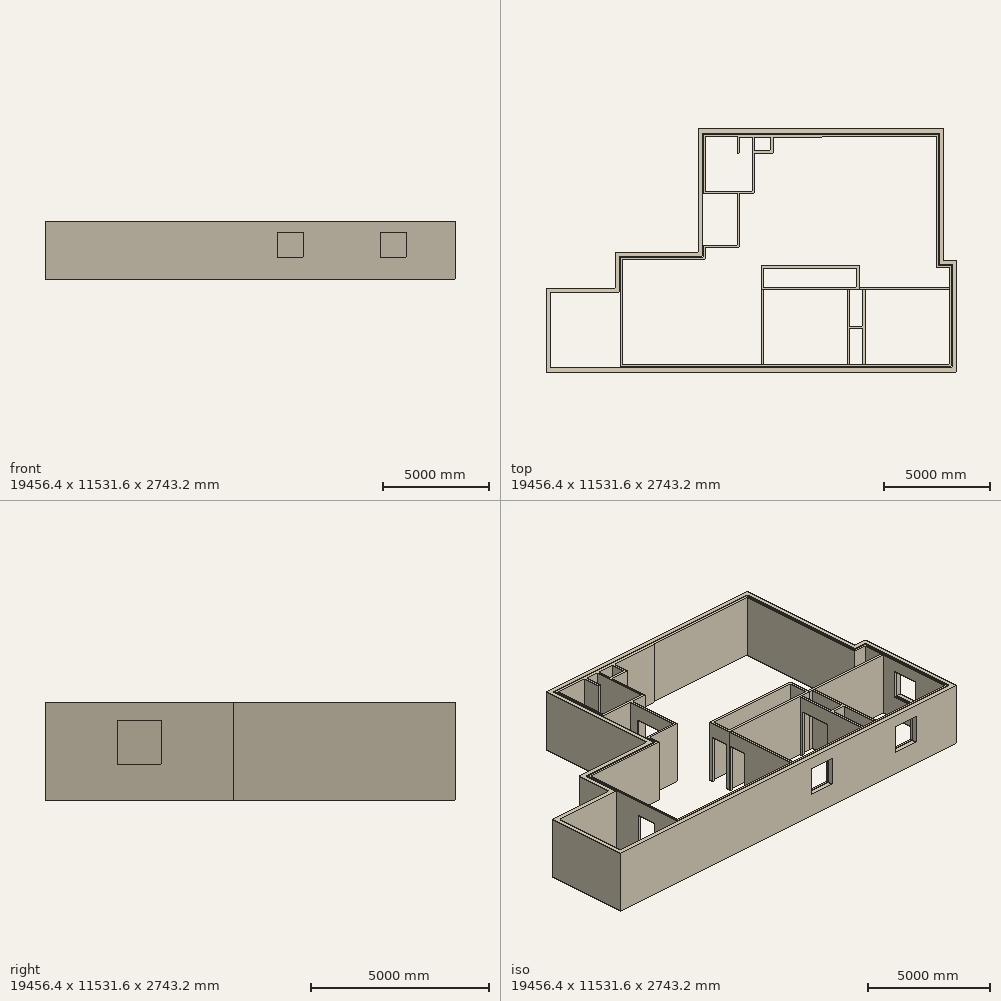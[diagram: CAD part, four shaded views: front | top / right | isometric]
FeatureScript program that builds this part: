
annotation { "Feature Type Name" : "Feature", "Feature Type Description" : "" }
export const myFeature = defineFeature(function(context is Context, id is Id, definition is map)
    precondition{}
    {
        {
            var Q0;
            Q0=qCreatedBy(makeId("Top.planeOp"),FACE);
            var sketch = newSketch(context, id + "F0", { "sketchPlane" : qUnion([Q0])});
            skLineSegment(sketch, "E0.bottom", {"start": v(0, 0) * mm, "end": v(19050, 0) * mm});
            skLineSegment(sketch, "E0.top", {"start": v(7213.6, 11125.2) * mm, "end": v(18440.4, 11125.2) * mm});
            skLineSegment(sketch, "E0.left", {"start": v(0, 0) * mm, "end": v(0, 3556) * mm});
            skLineSegment(sketch, "E0.right", {"start": v(19050, 0) * mm, "end": v(19050, 4876.8) * mm});
            skLineSegment(sketch, "E1", {"start": v(18440.4, 11125.2) * mm, "end": v(18440.4, 4876.8) * mm});
            skLineSegment(sketch, "E2", {"start": v(18440.4, 4876.8) * mm, "end": v(19050, 4876.8) * mm});
            skLineSegment(sketch, "E3", {"start": v(7213.6, 11125.2) * mm, "end": v(7213.6, 5283.2) * mm});
            skLineSegment(sketch, "E4", {"start": v(7213.6, 5283.2) * mm, "end": v(3276.6, 5283.2) * mm});
            skLineSegment(sketch, "E5", {"start": v(3276.6, 5283.2) * mm, "end": v(3276.6, 3556) * mm});
            skLineSegment(sketch, "E6", {"start": v(3276.6, 3556) * mm, "end": v(0, 3556) * mm});
            skLineSegment(sketch, "E7.bottom", {"start": v(9994.9, 4826) * mm, "end": v(14630.4, 4826) * mm, "construction": true});
            skLineSegment(sketch, "E7.top", {"start": v(9994.9, 3708.4) * mm, "end": v(14630.4, 3708.4) * mm, "construction": true});
            skLineSegment(sketch, "E7.left", {"start": v(9994.9, 4826) * mm, "end": v(9994.9, 3708.4) * mm, "construction": true});
            skLineSegment(sketch, "E7.right", {"start": v(14630.4, 4826) * mm, "end": v(14630.4, 3708.4) * mm, "construction": true});
            skPoint(sketch, "E8", {"position": v(16916.4, 0) * mm});
            skPoint(sketch, "E9", {"position": v(15697.2, 0) * mm});
            skPoint(sketch, "E10", {"position": v(12039.6, 0) * mm});
            skPoint(sketch, "E11", {"position": v(10820.4, 0) * mm});
            skPoint(sketch, "E12", {"position": v(12039.6, 11125.2) * mm});
            skPoint(sketch, "E13", {"position": v(10820.4, 11125.2) * mm});
            skPoint(sketch, "E14", {"position": v(19050, 1828.8) * mm});
            skPoint(sketch, "E15", {"position": v(19050, 3048) * mm});
            skLineSegment(sketch, "E16.0", {"start": v(7010.4, 11328.4) * mm, "end": v(18643.6, 11328.4) * mm});
            skLineSegment(sketch, "E17.0", {"start": v(18643.6, 11328.4) * mm, "end": v(18643.6, 5080) * mm});
            skLineSegment(sketch, "E18.0", {"start": v(18643.6, 5080) * mm, "end": v(19253.2, 5080) * mm});
            skLineSegment(sketch, "E19.0", {"start": v(19253.2, -203.2) * mm, "end": v(19253.2, 5080) * mm});
            skLineSegment(sketch, "E20.0", {"start": v(-203.2, -203.2) * mm, "end": v(19253.2, -203.2) * mm});
            skLineSegment(sketch, "E21.0", {"start": v(-203.2, -203.2) * mm, "end": v(-203.2, 3759.2) * mm});
            skLineSegment(sketch, "E22.0", {"start": v(3073.4, 3759.2) * mm, "end": v(-203.2, 3759.2) * mm});
            skLineSegment(sketch, "E23.0", {"start": v(3073.4, 5486.4) * mm, "end": v(3073.4, 3759.2) * mm});
            skLineSegment(sketch, "E24.0", {"start": v(7010.4, 5486.4) * mm, "end": v(3073.4, 5486.4) * mm});
            skLineSegment(sketch, "E25.0", {"start": v(7010.4, 11328.4) * mm, "end": v(7010.4, 5486.4) * mm});
            skPoint(sketch, "E26", {"position": v(8585.2, 11010.9) * mm});
            skPoint(sketch, "E27", {"position": v(9309.1, 10909.3) * mm});
            skPoint(sketch, "E28", {"position": v(8534.4, 10604.5) * mm});
            skSolve(sketch);
        }
        {
            var Q0;
            Q0=qCreatedBy(makeId("Top.planeOp"),FACE);
            var sketch = newSketch(context, id + "F1", { "sketchPlane" : qUnion([Q0])});
            skLineSegment(sketch, "E29", {"start": v(10972.8, 12242.8) * mm, "end": v(10795, 11328.4) * mm});
            skLineSegment(sketch, "E30", {"start": v(10795, 11328.4) * mm, "end": v(12065, 11328.4) * mm});
            skLineSegment(sketch, "E31", {"start": v(12065, 11328.4) * mm, "end": v(11887.2, 12242.8) * mm});
            skLineSegment(sketch, "E32", {"start": v(11887.2, 12242.8) * mm, "end": v(10972.8, 12242.8) * mm});
            skLineSegment(sketch, "E33", {"start": v(10820.4, 11125.2) * mm, "end": v(12039.6, 11125.2) * mm, "construction": true});
            skLineSegment(sketch, "E34", {"start": v(11430, 12242.8) * mm, "end": v(11430, 11125.2) * mm, "construction": true});
            skLineSegment(sketch, "E35", {"start": v(19050, 1828.8) * mm, "end": v(19050, 3048) * mm, "construction": true});
            skLineSegment(sketch, "E36", {"start": v(19253.2, 3073.4) * mm, "end": v(19253.2, 1803.4) * mm});
            skLineSegment(sketch, "E37", {"start": v(19253.2, 1803.4) * mm, "end": v(20167.6, 1981.2) * mm});
            skLineSegment(sketch, "E38", {"start": v(20167.6, 1981.2) * mm, "end": v(20167.6, 2895.6) * mm});
            skLineSegment(sketch, "E39", {"start": v(20167.6, 2895.6) * mm, "end": v(19253.2, 3073.4) * mm});
            skLineSegment(sketch, "E40", {"start": v(19050, 2438.4) * mm, "end": v(19253.2, 2438.4) * mm, "construction": true});
            skLineSegment(sketch, "E41", {"start": v(15697.2, 0) * mm, "end": v(16916.4, 0) * mm, "construction": true});
            skLineSegment(sketch, "E42", {"start": v(16306.8, 0) * mm, "end": v(16306.8, -203.2) * mm, "construction": true});
            skLineSegment(sketch, "E43", {"start": v(15671.8, -203.2) * mm, "end": v(16941.8, -203.2) * mm});
            skLineSegment(sketch, "E44", {"start": v(16941.8, -203.2) * mm, "end": v(16764, -1117.6) * mm});
            skLineSegment(sketch, "E45", {"start": v(16764, -1117.6) * mm, "end": v(15849.6, -1117.6) * mm});
            skLineSegment(sketch, "E46", {"start": v(15849.6, -1117.6) * mm, "end": v(15671.8, -203.2) * mm});
            skLineSegment(sketch, "E47", {"start": v(10820.4, 0) * mm, "end": v(12039.6, 0) * mm, "construction": true});
            skLineSegment(sketch, "E48", {"start": v(10795, -203.2) * mm, "end": v(10972.8, -1117.6) * mm});
            skLineSegment(sketch, "E49", {"start": v(10972.8, -1117.6) * mm, "end": v(11887.2, -1117.6) * mm});
            skLineSegment(sketch, "E50", {"start": v(11887.2, -1117.6) * mm, "end": v(12065, -203.2) * mm});
            skLineSegment(sketch, "E51", {"start": v(12065, -203.2) * mm, "end": v(10795, -203.2) * mm});
            skLineSegment(sketch, "E52", {"start": v(11430, 0) * mm, "end": v(11430, -203.2) * mm, "construction": true});
            skSolve(sketch);
        }
        {
            var Q0;
            Q0=makeQuery(id+"F0.imprint","IMPRINT",FACE,{"disambiguationData":[TD([[makeQuery(id+"F0.imprint","IMPRINT",EDGE,{"derivedFrom":sQuery(id+"F0.wireOp",EDGE,"E0.bottom")}),-1.0]])]});
            extrude(context, id + "F2", {"entities" : qUnion([Q0]), "depth" : 2743.2 * mm});
        }
        {
            var Q0;
            Q0=qCreatedBy(makeId("Top.planeOp"),FACE);
            var sketch = newSketch(context, id + "F3", { "sketchPlane" : qUnion([Q0])});
            skLineSegment(sketch, "E53.bottom", {"start": v(10096.5, 4724.4) * mm, "end": v(14528.8, 4724.4) * mm});
            skLineSegment(sketch, "E53.top", {"start": v(10096.5, 3810) * mm, "end": v(14528.8, 3810) * mm});
            skLineSegment(sketch, "E53.left", {"start": v(10096.5, 4724.4) * mm, "end": v(10096.5, 3810) * mm});
            skLineSegment(sketch, "E53.right", {"start": v(14528.8, 4724.4) * mm, "end": v(14528.8, 3810) * mm});
            skLineSegment(sketch, "E54.bottom", {"start": v(9982.2, 4838.7) * mm, "end": v(14643.1, 4838.7) * mm});
            skLineSegment(sketch, "E54.top", {"start": v(9982.2, 3695.7) * mm, "end": v(14643.1, 3695.7) * mm});
            skLineSegment(sketch, "E54.left", {"start": v(9982.2, 4838.7) * mm, "end": v(9982.2, 3695.7) * mm});
            skLineSegment(sketch, "E54.right", {"start": v(14643.1, 4838.7) * mm, "end": v(14643.1, 3695.7) * mm});
            skSolve(sketch);
        }
        {
            var Q0;
            Q0=qSketchRegion(id+"F3",true);
            extrude(context, id + "F4", {"entities" : qUnion([Q0]), "depth" : 2743.2 * mm});
        }
        {
            var Q0;
            Q0=qCreatedBy(makeId("Top.planeOp"),FACE);
            var sketch = newSketch(context, id + "F5", { "sketchPlane" : qUnion([Q0])});
            skLineSegment(sketch, "E55", {"start": v(3314.7, 5245.1) * mm, "end": v(3314.7, 38.1) * mm});
            skLineSegment(sketch, "E56", {"start": v(3314.7, 38.1) * mm, "end": v(19011.9, 38.1) * mm});
            skLineSegment(sketch, "E57", {"start": v(19011.9, 38.1) * mm, "end": v(19011.9, 4838.7) * mm});
            skLineSegment(sketch, "E58", {"start": v(19011.9, 4838.7) * mm, "end": v(18402.3, 4838.7) * mm});
            skLineSegment(sketch, "E59", {"start": v(18402.3, 4838.7) * mm, "end": v(18402.3, 11087.1) * mm});
            skLineSegment(sketch, "E60", {"start": v(18402.3, 11087.1) * mm, "end": v(7251.7, 11087.1) * mm});
            skLineSegment(sketch, "E61", {"start": v(7251.7, 11087.1) * mm, "end": v(7251.7, 8280.4) * mm});
            skLineSegment(sketch, "E62", {"start": v(7251.7, 8280.4) * mm, "end": v(8839.2, 8280.4) * mm});
            skLineSegment(sketch, "E63", {"start": v(8839.2, 8280.4) * mm, "end": v(8839.2, 5791.2) * mm});
            skLineSegment(sketch, "E64", {"start": v(8839.2, 5791.2) * mm, "end": v(7251.7, 5791.2) * mm});
            skLineSegment(sketch, "E65", {"start": v(7251.7, 5791.2) * mm, "end": v(7251.7, 5245.1) * mm});
            skLineSegment(sketch, "E66", {"start": v(7251.7, 5245.1) * mm, "end": v(3314.7, 5245.1) * mm});
            skLineSegment(sketch, "E67.0", {"start": v(18300.7, 10985.5) * mm, "end": v(7353.3, 10985.5) * mm});
            skLineSegment(sketch, "E67.1", {"start": v(7353.3, 5689.6) * mm, "end": v(7353.3, 5143.5) * mm});
            skLineSegment(sketch, "E67.2", {"start": v(8940.8, 5689.6) * mm, "end": v(7353.3, 5689.6) * mm});
            skLineSegment(sketch, "E67.3", {"start": v(8940.8, 8382) * mm, "end": v(8940.8, 5689.6) * mm});
            skLineSegment(sketch, "E67.4", {"start": v(7353.3, 8382) * mm, "end": v(8940.8, 8382) * mm});
            skLineSegment(sketch, "E67.5", {"start": v(7353.3, 5143.5) * mm, "end": v(3416.3, 5143.5) * mm});
            skLineSegment(sketch, "E67.6", {"start": v(7353.3, 10985.5) * mm, "end": v(7353.3, 8382) * mm});
            skLineSegment(sketch, "E67.7", {"start": v(3416.3, 5143.5) * mm, "end": v(3416.3, 139.7) * mm});
            skLineSegment(sketch, "E67.8", {"start": v(3416.3, 139.7) * mm, "end": v(18910.3, 139.7) * mm});
            skLineSegment(sketch, "E67.9", {"start": v(18910.3, 139.7) * mm, "end": v(18910.3, 4737.1) * mm});
            skLineSegment(sketch, "E67.10", {"start": v(18910.3, 4737.1) * mm, "end": v(18300.7, 4737.1) * mm});
            skLineSegment(sketch, "E67.11", {"start": v(18300.7, 4737.1) * mm, "end": v(18300.7, 10985.5) * mm});
            skSolve(sketch);
        }
        {
            var Q0;
            Q0=qSketchRegion(id+"F5",true);
            extrude(context, id + "F6", {"entities" : qUnion([Q0]), "depth" : 2743.2 * mm});
        }
        {
            var Q0;
            Q0=qCreatedBy(makeId("Top.planeOp"),FACE);
            var sketch = newSketch(context, id + "F7", { "sketchPlane" : qUnion([Q0])});
            skLineSegment(sketch, "E68", {"start": v(8940.8, 8382) * mm, "end": v(9569.45, 8382) * mm});
            skLineSegment(sketch, "E69", {"start": v(9569.45, 8382) * mm, "end": v(9569.45, 10934.7) * mm});
            skLineSegment(sketch, "E70", {"start": v(9683.75, 10934.7) * mm, "end": v(9683.75, 10299.7) * mm});
            skLineSegment(sketch, "E71", {"start": v(9683.75, 8280.4) * mm, "end": v(8940.8, 8280.4) * mm});
            skLineSegment(sketch, "E72", {"start": v(8940.8, 8280.4) * mm, "end": v(8940.8, 8382) * mm});
            skLineSegment(sketch, "E73.bottom", {"start": v(8845.55, 10934.7) * mm, "end": v(8959.85, 10934.7) * mm});
            skLineSegment(sketch, "E73.top", {"start": v(8845.55, 10172.7) * mm, "end": v(8959.85, 10172.7) * mm});
            skLineSegment(sketch, "E73.left", {"start": v(8845.55, 10934.7) * mm, "end": v(8845.55, 10172.7) * mm});
            skLineSegment(sketch, "E73.right", {"start": v(8959.85, 10934.7) * mm, "end": v(8959.85, 10172.7) * mm});
            skLineSegment(sketch, "E74", {"start": v(10560.05, 10934.7) * mm, "end": v(10560.05, 10185.4) * mm});
            skLineSegment(sketch, "E75", {"start": v(10560.05, 10185.4) * mm, "end": v(9683.75, 10185.4) * mm});
            skLineSegment(sketch, "E76", {"start": v(9683.75, 10299.7) * mm, "end": v(10445.75, 10299.7) * mm});
            skLineSegment(sketch, "E77", {"start": v(10445.75, 10299.7) * mm, "end": v(10445.75, 10934.7) * mm});
            skLineSegment(sketch, "E78.bottom", {"start": v(8845.55, 10985.5) * mm, "end": v(12903.2, 10985.5) * mm});
            skLineSegment(sketch, "E78.top", {"start": v(8845.55, 10934.7) * mm, "end": v(9569.45, 10934.7) * mm});
            skLineSegment(sketch, "E78.left", {"start": v(8845.55, 10985.5) * mm, "end": v(8845.55, 10934.7) * mm});
            skLineSegment(sketch, "E78.right", {"start": v(12903.2, 10985.5) * mm, "end": v(12903.2, 10934.7) * mm});
            skLineSegment(sketch, "E79.trimOffspring", {"start": v(9683.75, 10185.4) * mm, "end": v(9683.75, 8280.4) * mm});
            skLineSegment(sketch, "E80.trimOffspring", {"start": v(10560.05, 10934.7) * mm, "end": v(12903.2, 10934.7) * mm});
            skLineSegment(sketch, "E81.trimOffspring", {"start": v(9683.75, 10934.7) * mm, "end": v(10445.75, 10934.7) * mm});
            skPoint(sketch, "E82", {"position": v(10972.8, 10934.7) * mm});
            skPoint(sketch, "E83", {"position": v(11887.2, 10934.7) * mm});
            skPoint(sketch, "E84", {"position": v(12496.8, 10934.7) * mm});
            skLineSegment(sketch, "E85.bottom", {"start": v(10560.05, 10934.7) * mm, "end": v(10972.8, 10934.7) * mm, "construction": true});
            skLineSegment(sketch, "E85.top", {"start": v(10560.05, 10325.1) * mm, "end": v(10972.8, 10325.1) * mm, "construction": true});
            skLineSegment(sketch, "E85.left", {"start": v(10560.05, 10934.7) * mm, "end": v(10560.05, 10325.1) * mm, "construction": true});
            skLineSegment(sketch, "E85.right", {"start": v(10972.8, 10934.7) * mm, "end": v(10972.8, 10325.1) * mm, "construction": true});
            skLineSegment(sketch, "E86.bottom", {"start": v(10972.8, 10934.7) * mm, "end": v(11887.2, 10934.7) * mm, "construction": true});
            skLineSegment(sketch, "E86.top", {"start": v(10972.8, 10325.1) * mm, "end": v(11887.2, 10325.1) * mm, "construction": true});
            skLineSegment(sketch, "E86.right", {"start": v(11887.2, 10934.7) * mm, "end": v(11887.2, 10325.1) * mm, "construction": true});
            skLineSegment(sketch, "E87.bottom", {"start": v(11887.2, 10934.7) * mm, "end": v(12496.8, 10934.7) * mm, "construction": true});
            skLineSegment(sketch, "E87.top", {"start": v(11887.2, 10325.1) * mm, "end": v(12496.8, 10325.1) * mm, "construction": true});
            skLineSegment(sketch, "E87.right", {"start": v(12496.8, 10934.7) * mm, "end": v(12496.8, 10325.1) * mm, "construction": true});
            skLineSegment(sketch, "E88.bottom", {"start": v(12496.8, 10934.7) * mm, "end": v(12903.2, 10934.7) * mm, "construction": true});
            skLineSegment(sketch, "E88.top", {"start": v(12496.8, 10325.1) * mm, "end": v(12903.2, 10325.1) * mm, "construction": true});
            skLineSegment(sketch, "E88.right", {"start": v(12903.2, 10934.7) * mm, "end": v(12903.2, 10325.1) * mm, "construction": true});
            skPoint(sketch, "E89", {"position": v(11430, 10325.1) * mm});
            skSolve(sketch);
        }
        {
            var Q0;
            Q0=qSketchRegion(id+"F7",true);
            var Q1;
            Q1=makeQuery(id+"F2.opExtrude","CAP_FACE",FACE,{"disambiguationData":[OSD([sQuery(id+"F0.wireOp",EDGE,"E0.bottom"),sQuery(id+"F0.wireOp",EDGE,"E0.top"),sQuery(id+"F0.wireOp",EDGE,"E0.left"),sQuery(id+"F0.wireOp",EDGE,"E0.right"),sQuery(id+"F0.wireOp",EDGE,"E1"),sQuery(id+"F0.wireOp",EDGE,"E2"),sQuery(id+"F0.wireOp",EDGE,"E3"),sQuery(id+"F0.wireOp",EDGE,"E4"),sQuery(id+"F0.wireOp",EDGE,"E5"),sQuery(id+"F0.wireOp",EDGE,"E6"),sQuery(id+"F0.wireOp",EDGE,"E16.0"),sQuery(id+"F0.wireOp",EDGE,"E17.0"),sQuery(id+"F0.wireOp",EDGE,"E18.0"),sQuery(id+"F0.wireOp",EDGE,"E19.0"),sQuery(id+"F0.wireOp",EDGE,"E20.0"),sQuery(id+"F0.wireOp",EDGE,"E21.0"),sQuery(id+"F0.wireOp",EDGE,"E22.0"),sQuery(id+"F0.wireOp",EDGE,"E23.0"),sQuery(id+"F0.wireOp",EDGE,"E24.0"),sQuery(id+"F0.wireOp",EDGE,"E25.0")])],"isStart":false});
            extrude(context, id + "F8", {"entities" : qUnion([Q0]), "operationType" : NewBodyOperationType.ADD, "endBound" : BoundingType.UP_TO_SURFACE, "endBoundEntityFace" : qUnion([Q1]), "depth" : 25.4 * mm});
        }
        {
            var Q0;
            Q0=qCreatedBy(makeId("Top.planeOp"),FACE);
            var sketch = newSketch(context, id + "F9", { "sketchPlane" : qUnion([Q0])});
            skLineSegment(sketch, "E90.bottom", {"start": v(9982.2, 3695.7) * mm, "end": v(10096.5, 3695.7) * mm});
            skLineSegment(sketch, "E90.top", {"start": v(9982.2, 139.7) * mm, "end": v(10096.5, 139.7) * mm});
            skLineSegment(sketch, "E90.left", {"start": v(9982.2, 3695.7) * mm, "end": v(9982.2, 139.7) * mm});
            skLineSegment(sketch, "E90.right", {"start": v(10096.5, 3695.7) * mm, "end": v(10096.5, 139.7) * mm});
            skLineSegment(sketch, "E91.bottom", {"start": v(14643.1, 3695.7) * mm, "end": v(18910.3, 3695.7) * mm});
            skLineSegment(sketch, "E91.top", {"start": v(14643.1, 3810) * mm, "end": v(18910.3, 3810) * mm});
            skLineSegment(sketch, "E91.left", {"start": v(14643.1, 3695.7) * mm, "end": v(14643.1, 3810) * mm});
            skLineSegment(sketch, "E91.right", {"start": v(18910.3, 3695.7) * mm, "end": v(18910.3, 3810) * mm});
            skSolve(sketch);
        }
        {
            var Q0;
            Q0=qSketchRegion(id+"F9",true);
            extrude(context, id + "F10", {"entities" : qUnion([Q0]), "depth" : 2743.2 * mm});
        }
        {
            var Q0;
            Q0=makeQuery(id+"F2.opExtrude","SWEPT_FACE",FACE,{"disambiguationData":[OSD([sQuery(id+"F0.wireOp",EDGE,"E20.0")])]});
            var sketch = newSketch(context, id + "F11", { "sketchPlane" : qUnion([Q0])});
            skLineSegment(sketch, "E92.bottom", {"start": v(10820.4, 1016) * mm, "end": v(12039.6, 1016) * mm});
            skLineSegment(sketch, "E92.top", {"start": v(10820.4, 2235.2) * mm, "end": v(12039.6, 2235.2) * mm});
            skLineSegment(sketch, "E92.left", {"start": v(10820.4, 1016) * mm, "end": v(10820.4, 2235.2) * mm});
            skLineSegment(sketch, "E92.right", {"start": v(12039.6, 1016) * mm, "end": v(12039.6, 2235.2) * mm});
            skLineSegment(sketch, "E93.bottom", {"start": v(15697.2, 1016) * mm, "end": v(16916.4, 1016) * mm});
            skLineSegment(sketch, "E93.top", {"start": v(15697.2, 2235.2) * mm, "end": v(16916.4, 2235.2) * mm});
            skLineSegment(sketch, "E93.left", {"start": v(15697.2, 1016) * mm, "end": v(15697.2, 2235.2) * mm});
            skLineSegment(sketch, "E93.right", {"start": v(16916.4, 1016) * mm, "end": v(16916.4, 2235.2) * mm});
            skSolve(sketch);
        }
        {
            var Q0;
            Q0=qSketchRegion(id+"F11",true);
            var Q1;
            Q1=makeQuery(id+"F6.opExtrude","SWEPT_FACE",FACE,{"disambiguationData":[OSD([sQuery(id+"F5.wireOp",EDGE,"E67.8")])]});
            extrude(context, id + "F12", {"entities" : qUnion([Q0]), "operationType" : NewBodyOperationType.REMOVE, "endBound" : BoundingType.UP_TO_SURFACE, "oppositeDirection" : true, "endBoundEntityFace" : qUnion([Q1]), "depth" : 25.4 * mm});
        }
        {
            var Q0;
            Q0=qCreatedBy(makeId("Top.planeOp"),FACE);
            var sketch = newSketch(context, id + "F13", { "sketchPlane" : qUnion([Q0])});
            skLineSegment(sketch, "E94", {"start": v(10096.5, 1917.7) * mm, "end": v(14503.4, 1917.7) * mm, "construction": true});
            skLineSegment(sketch, "E95", {"start": v(14503.4, 1917.7) * mm, "end": v(18910.3, 1917.7) * mm, "construction": true});
            skLineSegment(sketch, "E96", {"start": v(14503.4, 3695.7) * mm, "end": v(14503.4, 139.7) * mm, "construction": true});
            skLineSegment(sketch, "E97.bottom", {"start": v(14084.3, 3695.7) * mm, "end": v(14198.6, 3695.7) * mm});
            skLineSegment(sketch, "E97.top", {"start": v(14084.3, 139.7) * mm, "end": v(14198.6, 139.7) * mm});
            skLineSegment(sketch, "E97.left", {"start": v(14084.3, 3695.7) * mm, "end": v(14084.3, 139.7) * mm});
            skLineSegment(sketch, "E97.right", {"start": v(14198.6, 3695.7) * mm, "end": v(14198.6, 1974.85) * mm});
            skLineSegment(sketch, "E98.bottom", {"start": v(14808.2, 3695.7) * mm, "end": v(14922.5, 3695.7) * mm});
            skLineSegment(sketch, "E98.top", {"start": v(14808.2, 139.7) * mm, "end": v(14922.5, 139.7) * mm});
            skLineSegment(sketch, "E98.left", {"start": v(14808.2, 3695.7) * mm, "end": v(14808.2, 1974.85) * mm});
            skLineSegment(sketch, "E98.right", {"start": v(14922.5, 3695.7) * mm, "end": v(14922.5, 139.7) * mm});
            skLineSegment(sketch, "E99.bottom", {"start": v(14198.6, 1974.85) * mm, "end": v(14808.2, 1974.85) * mm});
            skLineSegment(sketch, "E99.top", {"start": v(14198.6, 1860.55) * mm, "end": v(14808.2, 1860.55) * mm});
            skPoint(sketch, "E100", {"position": v(14503.4, 1974.85) * mm});
            skLineSegment(sketch, "E101.trimOffspring", {"start": v(14808.2, 1860.55) * mm, "end": v(14808.2, 139.7) * mm});
            skLineSegment(sketch, "E102", {"start": v(14198.6, 1860.55) * mm, "end": v(14198.6, 139.7) * mm});
            skSolve(sketch);
        }
        {
            var Q0;
            Q0=qSketchRegion(id+"F13",true);
            var Q1;
            Q1=makeQuery(id+"F2.opExtrude","CAP_FACE",FACE,{"disambiguationData":[OSD([sQuery(id+"F0.wireOp",EDGE,"E0.bottom"),sQuery(id+"F0.wireOp",EDGE,"E0.top"),sQuery(id+"F0.wireOp",EDGE,"E0.left"),sQuery(id+"F0.wireOp",EDGE,"E0.right"),sQuery(id+"F0.wireOp",EDGE,"E1"),sQuery(id+"F0.wireOp",EDGE,"E2"),sQuery(id+"F0.wireOp",EDGE,"E3"),sQuery(id+"F0.wireOp",EDGE,"E4"),sQuery(id+"F0.wireOp",EDGE,"E5"),sQuery(id+"F0.wireOp",EDGE,"E6"),sQuery(id+"F0.wireOp",EDGE,"E16.0"),sQuery(id+"F0.wireOp",EDGE,"E17.0"),sQuery(id+"F0.wireOp",EDGE,"E18.0"),sQuery(id+"F0.wireOp",EDGE,"E19.0"),sQuery(id+"F0.wireOp",EDGE,"E20.0"),sQuery(id+"F0.wireOp",EDGE,"E21.0"),sQuery(id+"F0.wireOp",EDGE,"E22.0"),sQuery(id+"F0.wireOp",EDGE,"E23.0"),sQuery(id+"F0.wireOp",EDGE,"E24.0"),sQuery(id+"F0.wireOp",EDGE,"E25.0")])],"isStart":false});
            extrude(context, id + "F14", {"entities" : qUnion([Q0]), "endBound" : BoundingType.UP_TO_SURFACE, "endBoundEntityFace" : qUnion([Q1]), "depth" : 25.4 * mm});
        }
        {
            var Q0;
            Q0=makeQuery(id+"F14.opExtrude","SWEPT_FACE",FACE,{"disambiguationData":[OSD([sQuery(id+"F13.wireOp",EDGE,"E98.right")])]});
            var sketch = newSketch(context, id + "F15", { "sketchPlane" : qUnion([Q0])});
            skLineSegment(sketch, "E103.bottom", {"start": v(257.17, 0) * mm, "end": v(1743.07, 0) * mm});
            skLineSegment(sketch, "E103.top", {"start": v(257.17, 2082.8) * mm, "end": v(1743.07, 2082.8) * mm});
            skLineSegment(sketch, "E103.left", {"start": v(257.17, 0) * mm, "end": v(257.17, 2082.8) * mm});
            skLineSegment(sketch, "E103.right", {"start": v(1743.07, 0) * mm, "end": v(1743.07, 2082.8) * mm});
            skLineSegment(sketch, "E104", {"start": v(1743.07, 2082.8) * mm, "end": v(1860.55, 2082.8) * mm, "construction": true});
            skLineSegment(sketch, "E105", {"start": v(257.17, 2082.8) * mm, "end": v(139.7, 2082.8) * mm, "construction": true});
            skSolve(sketch);
        }
        {
            var Q0;
            Q0=qSketchRegion(id+"F15",true);
            extrude(context, id + "F16", {"entities" : qUnion([Q0]), "operationType" : NewBodyOperationType.REMOVE, "endBound" : BoundingType.UP_TO_NEXT, "oppositeDirection" : true, "depth" : 25.4 * mm});
        }
        {
            var Q0;
            Q0=makeQuery(id+"F14.opExtrude","SWEPT_FACE",FACE,{"disambiguationData":[OSD([sQuery(id+"F13.wireOp",EDGE,"E97.left")])]});
            var sketch = newSketch(context, id + "F17", { "sketchPlane" : qUnion([Q0])});
            skLineSegment(sketch, "E106.bottom", {"start": v(-3578.23, 0) * mm, "end": v(-2092.32, 0) * mm});
            skLineSegment(sketch, "E106.top", {"start": v(-3578.23, 2082.8) * mm, "end": v(-2092.32, 2082.8) * mm});
            skLineSegment(sketch, "E106.left", {"start": v(-3578.23, 0) * mm, "end": v(-3578.23, 2082.8) * mm});
            skLineSegment(sketch, "E106.right", {"start": v(-2092.32, 0) * mm, "end": v(-2092.32, 2082.8) * mm});
            skLineSegment(sketch, "E107", {"start": v(-3578.23, 2082.8) * mm, "end": v(-3695.7, 2082.8) * mm, "construction": true});
            skLineSegment(sketch, "E108", {"start": v(-2092.32, 2082.8) * mm, "end": v(-1974.85, 2082.8) * mm, "construction": true});
            skSolve(sketch);
        }
        {
            var Q0;
            Q0=qSketchRegion(id+"F17",true);
            extrude(context, id + "F18", {"entities" : qUnion([Q0]), "operationType" : NewBodyOperationType.REMOVE, "endBound" : BoundingType.UP_TO_NEXT, "oppositeDirection" : true, "depth" : 25.4 * mm});
        }
        {
            var Q0;
            Q0=qCreatedBy(makeId("Top.planeOp"),FACE);
            var sketch = newSketch(context, id + "F19", { "sketchPlane" : qUnion([Q0])});
            skArc(sketch, "E109", {"start": v(10096.5, 2844.8) * mm, "mid": v(10635.32, 3067.98) * mm, "end": v(10858.5, 3606.8) * mm, "construction": true});
            skArc(sketch, "E110", {"start": v(9982.2, 3886.2) * mm, "mid": v(9443.38, 4109.38) * mm, "end": v(9220.2, 4648.2) * mm, "construction": true});
            skLineSegment(sketch, "E111", {"start": v(10096.5, 3606.8) * mm, "end": v(10858.5, 3606.8) * mm, "construction": true});
            skLineSegment(sketch, "E112", {"start": v(10096.5, 3606.8) * mm, "end": v(10096.5, 2844.8) * mm, "construction": true});
            skLineSegment(sketch, "E113", {"start": v(9982.2, 3886.2) * mm, "end": v(9982.2, 4648.2) * mm, "construction": true});
            skLineSegment(sketch, "E114", {"start": v(9220.2, 4648.2) * mm, "end": v(9982.2, 4648.2) * mm, "construction": true});
            skLineSegment(sketch, "E115", {"start": v(9982.2, 4648.2) * mm, "end": v(9982.2, 4724.4) * mm, "construction": true});
            skLineSegment(sketch, "E116", {"start": v(9982.2, 3886.2) * mm, "end": v(9982.2, 3810) * mm, "construction": true});
            skArc(sketch, "E117", {"start": v(15836.9, 2933.7) * mm, "mid": v(16375.72, 3156.88) * mm, "end": v(16598.9, 3695.7) * mm, "construction": true});
            skArc(sketch, "E118", {"start": v(8940.8, 6985) * mm, "mid": v(9587.38, 6717.18) * mm, "end": v(9855.2, 6070.6) * mm, "construction": true});
            skArc(sketch, "E119", {"start": v(8940.8, 6985) * mm, "mid": v(9587.38, 7252.82) * mm, "end": v(9855.2, 7899.4) * mm, "construction": true});
            skLineSegment(sketch, "E120", {"start": v(8940.8, 7899.4) * mm, "end": v(9855.2, 7899.4) * mm, "construction": true});
            skLineSegment(sketch, "E121", {"start": v(8940.8, 6985) * mm, "end": v(8940.8, 7899.4) * mm, "construction": true});
            skLineSegment(sketch, "E122", {"start": v(8940.8, 6985) * mm, "end": v(8940.8, 6070.6) * mm, "construction": true});
            skLineSegment(sketch, "E123", {"start": v(8940.8, 6070.6) * mm, "end": v(9855.2, 6070.6) * mm, "construction": true});
            skLineSegment(sketch, "E124", {"start": v(15836.9, 2933.7) * mm, "end": v(15836.9, 3695.7) * mm, "construction": true});
            skLineSegment(sketch, "E125", {"start": v(15836.9, 3695.7) * mm, "end": v(16598.9, 3695.7) * mm, "construction": true});
            skArc(sketch, "E126", {"start": v(3416.3, 2273.3) * mm, "mid": v(4062.88, 2005.48) * mm, "end": v(4330.7, 1358.9) * mm, "construction": true});
            skLineSegment(sketch, "E127", {"start": v(3416.3, 2273.3) * mm, "end": v(3416.3, 1358.9) * mm, "construction": true});
            skLineSegment(sketch, "E128", {"start": v(3416.3, 1358.9) * mm, "end": v(4330.7, 1358.9) * mm, "construction": true});
            skArc(sketch, "E129", {"start": v(14643.1, 4673.6) * mm, "mid": v(15217.84, 4435.54) * mm, "end": v(15455.9, 3860.8) * mm, "construction": true});
            skLineSegment(sketch, "E130", {"start": v(15455.9, 3860.8) * mm, "end": v(14643.1, 3860.8) * mm, "construction": true});
            skLineSegment(sketch, "E131", {"start": v(14643.1, 3860.8) * mm, "end": v(14643.1, 4673.6) * mm, "construction": true});
            skLineSegment(sketch, "E132", {"start": v(14643.1, 4673.6) * mm, "end": v(14643.1, 4724.4) * mm, "construction": true});
            skLineSegment(sketch, "E133", {"start": v(14643.1, 3860.8) * mm, "end": v(14643.1, 3810) * mm, "construction": true});
            skArc(sketch, "E134", {"start": v(9569.45, 9220.2) * mm, "mid": v(9030.63, 8997.02) * mm, "end": v(8807.45, 8458.2) * mm, "construction": true});
            skLineSegment(sketch, "E135", {"start": v(8807.45, 8458.2) * mm, "end": v(9569.45, 8458.2) * mm, "construction": true});
            skLineSegment(sketch, "E136", {"start": v(9569.45, 8458.2) * mm, "end": v(9569.45, 9220.2) * mm, "construction": true});
            skArc(sketch, "E137", {"start": v(9759.95, 9575.8) * mm, "mid": v(10191, 9754.35) * mm, "end": v(10369.55, 10185.4) * mm, "construction": true});
            skLineSegment(sketch, "E138", {"start": v(9759.95, 9575.8) * mm, "end": v(9759.95, 10185.4) * mm, "construction": true});
            skLineSegment(sketch, "E139", {"start": v(9759.95, 10185.4) * mm, "end": v(10369.55, 10185.4) * mm, "construction": true});
            skSolve(sketch);
        }
        {
            var Q0;
            Q0=makeQuery(id+"F10.opExtrude","SWEPT_FACE",FACE,{"disambiguationData":[OSD([sQuery(id+"F9.wireOp",EDGE,"E90.left")])]});
            var sketch = newSketch(context, id + "F20", { "sketchPlane" : qUnion([Q0])});
            skLineSegment(sketch, "E140.bottom", {"start": v(-3606.8, 0) * mm, "end": v(-2844.8, 0) * mm});
            skLineSegment(sketch, "E140.top", {"start": v(-3606.8, 2082.8) * mm, "end": v(-2844.8, 2082.8) * mm});
            skLineSegment(sketch, "E140.left", {"start": v(-3606.8, 0) * mm, "end": v(-3606.8, 2082.8) * mm});
            skLineSegment(sketch, "E140.right", {"start": v(-2844.8, 0) * mm, "end": v(-2844.8, 2082.8) * mm});
            skSolve(sketch);
        }
        {
            var Q0;
            Q0=qSketchRegion(id+"F20",true);
            extrude(context, id + "F21", {"entities" : qUnion([Q0]), "operationType" : NewBodyOperationType.REMOVE, "endBound" : BoundingType.UP_TO_NEXT, "oppositeDirection" : true, "depth" : 25.4 * mm});
        }
        {
            var Q0;
            Q0=makeQuery(id+"F4.opExtrude","SWEPT_FACE",FACE,{"disambiguationData":[OSD([sQuery(id+"F3.wireOp",EDGE,"E54.left")])]});
            var sketch = newSketch(context, id + "F22", { "sketchPlane" : qUnion([Q0])});
            skLineSegment(sketch, "E141.bottom", {"start": v(-4648.2, 0) * mm, "end": v(-3886.2, 0) * mm});
            skLineSegment(sketch, "E141.top", {"start": v(-4648.2, 2082.8) * mm, "end": v(-3886.2, 2082.8) * mm});
            skLineSegment(sketch, "E141.left", {"start": v(-4648.2, 0) * mm, "end": v(-4648.2, 2082.8) * mm});
            skLineSegment(sketch, "E141.right", {"start": v(-3886.2, 0) * mm, "end": v(-3886.2, 2082.8) * mm});
            skSolve(sketch);
        }
        {
            var Q0;
            Q0=qSketchRegion(id+"F22",true);
            var Q1;
            Q1=makeQuery(id+"F4.opExtrude","SWEPT_FACE",FACE,{"disambiguationData":[OSD([sQuery(id+"F3.wireOp",EDGE,"E54.right")])]});
            extrude(context, id + "F23", {"entities" : qUnion([Q0]), "operationType" : NewBodyOperationType.REMOVE, "endBound" : BoundingType.UP_TO_SURFACE, "oppositeDirection" : true, "endBoundEntityFace" : qUnion([Q1]), "depth" : 25.4 * mm});
        }
        {
            var Q0;
            Q0=makeQuery(id+"F6.opExtrude","SWEPT_FACE",FACE,{"disambiguationData":[OSD([sQuery(id+"F5.wireOp",EDGE,"E67.3")])]});
            var sketch = newSketch(context, id + "F24", { "sketchPlane" : qUnion([Q0])});
            skLineSegment(sketch, "E142.bottom", {"start": v(6070.6, 0) * mm, "end": v(7899.4, 0) * mm});
            skLineSegment(sketch, "E142.top", {"start": v(6070.6, 2082.8) * mm, "end": v(7899.4, 2082.8) * mm});
            skLineSegment(sketch, "E142.left", {"start": v(6070.6, 0) * mm, "end": v(6070.6, 2082.8) * mm});
            skLineSegment(sketch, "E142.right", {"start": v(7899.4, 0) * mm, "end": v(7899.4, 2082.8) * mm});
            skSolve(sketch);
        }
        {
            var Q0;
            Q0=qSketchRegion(id+"F24",true);
            extrude(context, id + "F25", {"entities" : qUnion([Q0]), "operationType" : NewBodyOperationType.REMOVE, "endBound" : BoundingType.UP_TO_NEXT, "oppositeDirection" : true, "depth" : 25.4 * mm});
        }
        {
            var Q0;
            Q0=makeQuery(id+"F6.opExtrude","SWEPT_FACE",FACE,{"disambiguationData":[OSD([sQuery(id+"F5.wireOp",EDGE,"E67.7")])]});
            var sketch = newSketch(context, id + "F26", { "sketchPlane" : qUnion([Q0])});
            skLineSegment(sketch, "E143.bottom", {"start": v(1358.9, 0) * mm, "end": v(2273.3, 0) * mm});
            skLineSegment(sketch, "E143.top", {"start": v(1358.9, 2082.8) * mm, "end": v(2273.3, 2082.8) * mm});
            skLineSegment(sketch, "E143.left", {"start": v(1358.9, 0) * mm, "end": v(1358.9, 2082.8) * mm});
            skLineSegment(sketch, "E143.right", {"start": v(2273.3, 0) * mm, "end": v(2273.3, 2082.8) * mm});
            skSolve(sketch);
        }
        {
            var Q0;
            Q0=qSketchRegion(id+"F26",true);
            extrude(context, id + "F27", {"entities" : qUnion([Q0]), "operationType" : NewBodyOperationType.REMOVE, "endBound" : BoundingType.UP_TO_NEXT, "oppositeDirection" : true, "depth" : 25.4 * mm});
        }
        {
            var Q0;
            Q0=makeQuery(id+"F2.opExtrude","SWEPT_FACE",FACE,{"disambiguationData":[OSD([sQuery(id+"F0.wireOp",EDGE,"E19.0")])]});
            var sketch = newSketch(context, id + "F28", { "sketchPlane" : qUnion([Q0])});
            skLineSegment(sketch, "E144.bottom", {"start": v(1828.8, 2235.2) * mm, "end": v(3048, 2235.2) * mm});
            skLineSegment(sketch, "E144.top", {"start": v(1828.8, 1016) * mm, "end": v(3048, 1016) * mm});
            skLineSegment(sketch, "E144.left", {"start": v(1828.8, 2235.2) * mm, "end": v(1828.8, 1016) * mm});
            skLineSegment(sketch, "E144.right", {"start": v(3048, 2235.2) * mm, "end": v(3048, 1016) * mm});
            skSolve(sketch);
        }
        {
            var Q0;
            Q0=qSketchRegion(id+"F28",true);
            var Q1;
            Q1=makeQuery(id+"F6.opExtrude","SWEPT_FACE",FACE,{"disambiguationData":[OSD([sQuery(id+"F5.wireOp",EDGE,"E67.9")])]});
            extrude(context, id + "F29", {"entities" : qUnion([Q0]), "operationType" : NewBodyOperationType.REMOVE, "endBound" : BoundingType.UP_TO_SURFACE, "oppositeDirection" : true, "endBoundEntityFace" : qUnion([Q1]), "depth" : 25.4 * mm});
        }
        {
            var Q0;
            Q0=makeQuery(id+"F2.opExtrude","SWEPT_FACE",FACE,{"disambiguationData":[OSD([sQuery(id+"F0.wireOp",EDGE,"E16.0")])]});
            var sketch = newSketch(context, id + "F30", { "sketchPlane" : qUnion([Q0])});
            skLineSegment(sketch, "E145.bottom", {"start": v(-12039.6, 1016) * mm, "end": v(-10820.4, 1016) * mm});
            skLineSegment(sketch, "E145.top", {"start": v(-12039.6, 2235.2) * mm, "end": v(-10820.4, 2235.2) * mm});
            skLineSegment(sketch, "E145.left", {"start": v(-12039.6, 1016) * mm, "end": v(-12039.6, 2235.2) * mm});
            skLineSegment(sketch, "E145.right", {"start": v(-10820.4, 1016) * mm, "end": v(-10820.4, 2235.2) * mm});
            skSolve(sketch);
        }
        {
            var Q0;
            Q0=qSketchRegion(id+"F30",true);
            var Q1;
            Q1=makeQuery(id+"F6.opExtrude","SWEPT_FACE",FACE,{"disambiguationData":[OSD([sQuery(id+"F5.wireOp",EDGE,"E67.0")])]});
            extrude(context, id + "F31", {"entities" : qUnion([Q0]), "operationType" : NewBodyOperationType.REMOVE, "endBound" : BoundingType.UP_TO_SURFACE, "oppositeDirection" : true, "endBoundEntityFace" : qUnion([Q1]), "depth" : 25.4 * mm});
        }
        {
            var Q0;
            Q0=qCreatedBy(makeId("Top.planeOp"),FACE);
            var sketch = newSketch(context, id + "F32", { "sketchPlane" : qUnion([Q0])});
            skLineSegment(sketch, "E146.bottom", {"start": v(7353.3, 10985.5) * mm, "end": v(8845.55, 10985.5) * mm});
            skLineSegment(sketch, "E146.top", {"start": v(7353.3, 10261.6) * mm, "end": v(8845.55, 10261.6) * mm});
            skLineSegment(sketch, "E146.left", {"start": v(7353.3, 10985.5) * mm, "end": v(7353.3, 10261.6) * mm});
            skLineSegment(sketch, "E146.right", {"start": v(8845.55, 10985.5) * mm, "end": v(8845.55, 10261.6) * mm});
            skLineSegment(sketch, "E147.bottom", {"start": v(7378.7, 9956.8) * mm, "end": v(7556.5, 9956.8) * mm});
            skLineSegment(sketch, "E147.top", {"start": v(7378.7, 9550.4) * mm, "end": v(7556.5, 9550.4) * mm});
            skLineSegment(sketch, "E147.left", {"start": v(7378.7, 9956.8) * mm, "end": v(7378.7, 9550.4) * mm});
            skLineSegment(sketch, "E147.right", {"start": v(7556.5, 9956.8) * mm, "end": v(7556.5, 9550.4) * mm});
            skLineSegment(sketch, "E148", {"start": v(7556.5, 9753.6) * mm, "end": v(7823.2, 9753.6) * mm});
            skEllipse(sketch, "E149", {"center": v(7823.2, 9753.6) * mm, "majorRadius": 215.9 * mm, "minorRadius": 184.15 * mm, "majorAxis": v(1, 0)});
            skPoint(sketch, "E150", {"position": v(8039.1, 9753.6) * mm});
            skLineSegment(sketch, "E151.bottom", {"start": v(7353.3, 8382) * mm, "end": v(7912.1, 8382) * mm});
            skLineSegment(sketch, "E151.top", {"start": v(7353.3, 9347.2) * mm, "end": v(7912.1, 9347.2) * mm});
            skLineSegment(sketch, "E151.left", {"start": v(7353.3, 8382) * mm, "end": v(7353.3, 9347.2) * mm});
            skLineSegment(sketch, "E151.right", {"start": v(7912.1, 8382) * mm, "end": v(7912.1, 9347.2) * mm});
            skLineSegment(sketch, "E152", {"start": v(7353.3, 9347.2) * mm, "end": v(7912.1, 8382) * mm, "construction": true});
            skLineSegment(sketch, "E153", {"start": v(7353.3, 8382) * mm, "end": v(7912.1, 9347.2) * mm, "construction": true});
            skEllipse(sketch, "E154", {"center": v(7632.7, 8864.6) * mm, "majorRadius": 203.2 * mm, "minorRadius": 152.4 * mm, "majorAxis": v(0, 1), "construction": true});
            skLineSegment(sketch, "E155.bottom", {"start": v(10560.05, 10934.7) * mm, "end": v(12903.2, 10934.7) * mm});
            skLineSegment(sketch, "E155.top", {"start": v(10560.05, 10274.3) * mm, "end": v(12903.2, 10274.3) * mm});
            skLineSegment(sketch, "E155.left", {"start": v(10560.05, 10934.7) * mm, "end": v(10560.05, 10274.3) * mm});
            skLineSegment(sketch, "E155.right", {"start": v(12903.2, 10934.7) * mm, "end": v(12903.2, 10274.3) * mm});
            skLineSegment(sketch, "E156.bottom", {"start": v(12928.6, 10960.1) * mm, "end": v(13843, 10960.1) * mm});
            skLineSegment(sketch, "E156.top", {"start": v(12928.6, 10096.5) * mm, "end": v(13843, 10096.5) * mm});
            skLineSegment(sketch, "E156.left", {"start": v(12928.6, 10960.1) * mm, "end": v(12928.6, 10096.5) * mm});
            skLineSegment(sketch, "E156.right", {"start": v(13843, 10960.1) * mm, "end": v(13843, 10096.5) * mm});
            skLineSegment(sketch, "E157.bottom", {"start": v(11049, 10795) * mm, "end": v(11404.6, 10795) * mm});
            skLineSegment(sketch, "E157.top", {"start": v(11049, 10414) * mm, "end": v(11404.6, 10414) * mm});
            skLineSegment(sketch, "E157.left", {"start": v(11049, 10795) * mm, "end": v(11049, 10414) * mm});
            skLineSegment(sketch, "E157.right", {"start": v(11404.6, 10795) * mm, "end": v(11404.6, 10414) * mm});
            skLineSegment(sketch, "E158.bottom", {"start": v(11455.4, 10795) * mm, "end": v(11811, 10795) * mm});
            skLineSegment(sketch, "E158.top", {"start": v(11455.4, 10414) * mm, "end": v(11811, 10414) * mm});
            skLineSegment(sketch, "E158.left", {"start": v(11455.4, 10795) * mm, "end": v(11455.4, 10414) * mm});
            skLineSegment(sketch, "E158.right", {"start": v(11811, 10795) * mm, "end": v(11811, 10414) * mm});
            skLineSegment(sketch, "E159", {"start": v(11404.6, 10604.5) * mm, "end": v(11455.4, 10604.5) * mm, "construction": true});
            skPoint(sketch, "E160", {"position": v(11430, 10604.5) * mm});
            skLineSegment(sketch, "E161", {"start": v(11430, 10934.7) * mm, "end": v(11430, 10274.3) * mm, "construction": true});
            skLineSegment(sketch, "E162.bottom", {"start": v(8959.85, 10934.7) * mm, "end": v(9569.45, 10934.7) * mm});
            skLineSegment(sketch, "E162.top", {"start": v(8959.85, 10528.3) * mm, "end": v(9569.45, 10528.3) * mm});
            skLineSegment(sketch, "E162.left", {"start": v(8959.85, 10934.7) * mm, "end": v(8959.85, 10528.3) * mm});
            skLineSegment(sketch, "E162.right", {"start": v(9569.45, 10934.7) * mm, "end": v(9569.45, 10528.3) * mm});
            skEllipse(sketch, "E163", {"center": v(8099.43, 10623.55) * mm, "majorRadius": 609.6 * mm, "minorRadius": 279.4 * mm, "majorAxis": v(1, 0), "construction": true});
            skLineSegment(sketch, "E164", {"start": v(7353.3, 10985.5) * mm, "end": v(8845.55, 10261.6) * mm, "construction": true});
            skLineSegment(sketch, "E165", {"start": v(8845.55, 10985.5) * mm, "end": v(7353.3, 10261.6) * mm, "construction": true});
            skSolve(sketch);
        }
        {
            var Q0;
            Q0=makeQuery(id+"F8.opExtrude","SWEPT_FACE",FACE,{"disambiguationData":[OSD([sQuery(id+"F7.wireOp",EDGE,"E70")])]});
            var sketch = newSketch(context, id + "F33", { "sketchPlane" : qUnion([Q0])});
            skLineSegment(sketch, "E166.bottom", {"start": v(8458.2, 0) * mm, "end": v(9220.2, 0) * mm});
            skLineSegment(sketch, "E166.top", {"start": v(8458.2, 2082.8) * mm, "end": v(9220.2, 2082.8) * mm});
            skLineSegment(sketch, "E166.left", {"start": v(8458.2, 0) * mm, "end": v(8458.2, 2082.8) * mm});
            skLineSegment(sketch, "E166.right", {"start": v(9220.2, 0) * mm, "end": v(9220.2, 2082.8) * mm});
            skSolve(sketch);
        }
        {
            var Q0;
            Q0=qSketchRegion(id+"F33",true);
            extrude(context, id + "F34", {"entities" : qUnion([Q0]), "operationType" : NewBodyOperationType.REMOVE, "endBound" : BoundingType.UP_TO_NEXT, "oppositeDirection" : true, "depth" : 25.4 * mm});
        }
        {
            var Q0;
            Q0=makeQuery(id+"F8.opExtrude","SWEPT_FACE",FACE,{"disambiguationData":[OSD([sQuery(id+"F7.wireOp",EDGE,"E75")])]});
            var sketch = newSketch(context, id + "F35", { "sketchPlane" : qUnion([Q0])});
            skLineSegment(sketch, "E167.bottom", {"start": v(9759.95, 0) * mm, "end": v(10369.55, 0) * mm});
            skLineSegment(sketch, "E167.top", {"start": v(9759.95, 2082.8) * mm, "end": v(10369.55, 2082.8) * mm});
            skLineSegment(sketch, "E167.left", {"start": v(9759.95, 0) * mm, "end": v(9759.95, 2082.8) * mm});
            skLineSegment(sketch, "E167.right", {"start": v(10369.55, 0) * mm, "end": v(10369.55, 2082.8) * mm});
            skSolve(sketch);
        }
        {
            var Q0;
            Q0=qSketchRegion(id+"F35",true);
            extrude(context, id + "F36", {"entities" : qUnion([Q0]), "operationType" : NewBodyOperationType.REMOVE, "endBound" : BoundingType.UP_TO_NEXT, "oppositeDirection" : true, "depth" : 25.4 * mm});
        }
        {
            var Q0;
            Q0=makeQuery(id+"F2.opExtrude","CAP_FACE",FACE,{"disambiguationData":[OSD([sQuery(id+"F0.wireOp",EDGE,"E0.bottom"),sQuery(id+"F0.wireOp",EDGE,"E0.top"),sQuery(id+"F0.wireOp",EDGE,"E0.left"),sQuery(id+"F0.wireOp",EDGE,"E0.right"),sQuery(id+"F0.wireOp",EDGE,"E1"),sQuery(id+"F0.wireOp",EDGE,"E2"),sQuery(id+"F0.wireOp",EDGE,"E3"),sQuery(id+"F0.wireOp",EDGE,"E4"),sQuery(id+"F0.wireOp",EDGE,"E5"),sQuery(id+"F0.wireOp",EDGE,"E6"),sQuery(id+"F0.wireOp",EDGE,"E16.0"),sQuery(id+"F0.wireOp",EDGE,"E17.0"),sQuery(id+"F0.wireOp",EDGE,"E18.0"),sQuery(id+"F0.wireOp",EDGE,"E19.0"),sQuery(id+"F0.wireOp",EDGE,"E20.0"),sQuery(id+"F0.wireOp",EDGE,"E21.0"),sQuery(id+"F0.wireOp",EDGE,"E22.0"),sQuery(id+"F0.wireOp",EDGE,"E23.0"),sQuery(id+"F0.wireOp",EDGE,"E24.0"),sQuery(id+"F0.wireOp",EDGE,"E25.0")])],"isStart":false});
            var sketch = newSketch(context, id + "F37", { "sketchPlane" : qUnion([Q0])});
            skPoint(sketch, "E168", {"position": v(15836.9, 1054.1) * mm});
            skPoint(sketch, "E169", {"position": v(15836.9, 2781.3) * mm});
            skPoint(sketch, "E170", {"position": v(17995.9, 2781.3) * mm});
            skPoint(sketch, "E171", {"position": v(17995.9, 1054.1) * mm});
            skLineSegment(sketch, "E172.bottom", {"start": v(15836.9, 2781.3) * mm, "end": v(17995.9, 2781.3) * mm, "construction": true});
            skLineSegment(sketch, "E172.top", {"start": v(15836.9, 1054.1) * mm, "end": v(17995.9, 1054.1) * mm, "construction": true});
            skLineSegment(sketch, "E172.left", {"start": v(15836.9, 2781.3) * mm, "end": v(15836.9, 1054.1) * mm, "construction": true});
            skLineSegment(sketch, "E172.right", {"start": v(17995.9, 2781.3) * mm, "end": v(17995.9, 1054.1) * mm, "construction": true});
            skLineSegment(sketch, "E173.bottom", {"start": v(11010.9, 2781.3) * mm, "end": v(13169.9, 2781.3) * mm, "construction": true});
            skLineSegment(sketch, "E173.top", {"start": v(11010.9, 1054.1) * mm, "end": v(13169.9, 1054.1) * mm, "construction": true});
            skLineSegment(sketch, "E173.left", {"start": v(11010.9, 2781.3) * mm, "end": v(11010.9, 1054.1) * mm, "construction": true});
            skLineSegment(sketch, "E173.right", {"start": v(13169.9, 2781.3) * mm, "end": v(13169.9, 1054.1) * mm, "construction": true});
            skPoint(sketch, "E174", {"position": v(11010.9, 2781.3) * mm});
            skPoint(sketch, "E175", {"position": v(11010.9, 1054.1) * mm});
            skPoint(sketch, "E176", {"position": v(13169.9, 1054.1) * mm});
            skPoint(sketch, "E177", {"position": v(13169.9, 2781.3) * mm});
            skLineSegment(sketch, "E178", {"start": v(11010.9, 2781.3) * mm, "end": v(13169.9, 1054.1) * mm, "construction": true});
            skPoint(sketch, "E179", {"position": v(12090.4, 1917.7) * mm});
            skLineSegment(sketch, "E180", {"start": v(15836.9, 2781.3) * mm, "end": v(17995.9, 1054.1) * mm, "construction": true});
            skPoint(sketch, "E181", {"position": v(16916.4, 1917.7) * mm});
            skPoint(sketch, "E182", {"position": v(10064.75, 9880.6) * mm});
            skLineSegment(sketch, "E183", {"start": v(10064.75, 9880.6) * mm, "end": v(10064.75, 10185.4) * mm, "construction": true});
            skPoint(sketch, "E184", {"position": v(11430, 10629.9) * mm});
            skPoint(sketch, "E185", {"position": v(15557.5, 4273.55) * mm});
            skPoint(sketch, "E186", {"position": v(17820.22, 4273.55) * mm});
            skPoint(sketch, "E187", {"position": v(10598.15, 5722.94) * mm});
            skPoint(sketch, "E188", {"position": v(12860.87, 5722.94) * mm});
            skPoint(sketch, "E189", {"position": v(15123.58, 5722.94) * mm});
            skPoint(sketch, "E190", {"position": v(15123.58, 10071.1) * mm});
            skPoint(sketch, "E191", {"position": v(17386.3, 10071.1) * mm});
            skPoint(sketch, "E192", {"position": v(10598.15, 7172.32) * mm});
            skPoint(sketch, "E193", {"position": v(12860.87, 7172.32) * mm});
            skPoint(sketch, "E194", {"position": v(15123.58, 7172.32) * mm});
            skPoint(sketch, "E195", {"position": v(17386.3, 7172.32) * mm});
            skPoint(sketch, "E196", {"position": v(7556.5, 8864.6) * mm});
            skPoint(sketch, "E197", {"position": v(8099.43, 10623.55) * mm});
            skPoint(sketch, "E198", {"position": v(9264.65, 10172.7) * mm});
            skLineSegment(sketch, "E199", {"start": v(10598.15, 7172.32) * mm, "end": v(12860.87, 7172.32) * mm, "construction": true});
            skLineSegment(sketch, "E200", {"start": v(12860.87, 7172.32) * mm, "end": v(15123.58, 7172.32) * mm, "construction": true});
            skLineSegment(sketch, "E201", {"start": v(15123.58, 7172.32) * mm, "end": v(17386.3, 7172.32) * mm, "construction": true});
            skLineSegment(sketch, "E202", {"start": v(10598.15, 5722.94) * mm, "end": v(12860.87, 5722.94) * mm, "construction": true});
            skLineSegment(sketch, "E203", {"start": v(12860.87, 5722.94) * mm, "end": v(15123.58, 5722.94) * mm, "construction": true});
            skLineSegment(sketch, "E204", {"start": v(15123.58, 10071.1) * mm, "end": v(17386.3, 10071.1) * mm, "construction": true});
            skLineSegment(sketch, "E205", {"start": v(15557.5, 4273.55) * mm, "end": v(17820.22, 4273.55) * mm, "construction": true});
            skLineSegment(sketch, "E206", {"start": v(15123.58, 5722.94) * mm, "end": v(17386.3, 5722.94) * mm, "construction": true});
            skPoint(sketch, "E207", {"position": v(17386.3, 5722.94) * mm});
            skLineSegment(sketch, "E208", {"start": v(17386.3, 7172.32) * mm, "end": v(17386.3, 5722.94) * mm, "construction": true});
            skLineSegment(sketch, "E209", {"start": v(17386.3, 5722.94) * mm, "end": v(17386.3, 4273.55) * mm, "construction": true});
            skLineSegment(sketch, "E210", {"start": v(17820.22, 4273.55) * mm, "end": v(18910.3, 4273.55) * mm, "construction": true});
            skLineSegment(sketch, "E211", {"start": v(18910.3, 4737.1) * mm, "end": v(18910.3, 3810) * mm, "construction": true});
            skPoint(sketch, "E212", {"position": v(4330.7, 4229.1) * mm});
            skPoint(sketch, "E213", {"position": v(6699.25, 4229.1) * mm});
            skPoint(sketch, "E214", {"position": v(9067.8, 4229.1) * mm});
            skPoint(sketch, "E215", {"position": v(9067.8, 1054.1) * mm});
            skPoint(sketch, "E216", {"position": v(6699.25, 1054.1) * mm});
            skPoint(sketch, "E217", {"position": v(4330.7, 1054.1) * mm});
            skLineSegment(sketch, "E218", {"start": v(4330.7, 4229.1) * mm, "end": v(4330.7, 1054.1) * mm, "construction": true});
            skLineSegment(sketch, "E219", {"start": v(4330.7, 1054.1) * mm, "end": v(6699.25, 1054.1) * mm, "construction": true});
            skLineSegment(sketch, "E220", {"start": v(6699.25, 1054.1) * mm, "end": v(9067.8, 1054.1) * mm, "construction": true});
            skLineSegment(sketch, "E221", {"start": v(3416.3, 2641.6) * mm, "end": v(4330.7, 2641.6) * mm, "construction": true});
            skLineSegment(sketch, "E222", {"start": v(3416.3, 139.7) * mm, "end": v(9982.2, 139.7) * mm});
            skLineSegment(sketch, "E223", {"start": v(6699.25, 139.7) * mm, "end": v(6699.25, 1054.1) * mm, "construction": true});
            skPoint(sketch, "E224", {"position": v(6699.25, 2641.6) * mm});
            skPoint(sketch, "E225", {"position": v(9067.8, 2641.6) * mm});
            skPoint(sketch, "E226", {"position": v(4330.7, 2641.6) * mm});
            skPoint(sketch, "E227", {"position": v(10598.15, 8621.71) * mm});
            skPoint(sketch, "E228", {"position": v(12860.87, 8621.71) * mm});
            skPoint(sketch, "E229", {"position": v(15123.58, 8621.71) * mm});
            skPoint(sketch, "E230", {"position": v(17386.3, 8621.71) * mm});
            skLineSegment(sketch, "E231", {"start": v(17386.3, 7172.32) * mm, "end": v(17386.3, 8621.71) * mm, "construction": true});
            skLineSegment(sketch, "E232", {"start": v(17386.3, 8621.71) * mm, "end": v(17386.3, 10071.1) * mm, "construction": true});
            skLineSegment(sketch, "E233", {"start": v(10598.15, 8621.71) * mm, "end": v(12860.87, 8621.71) * mm, "construction": true});
            skLineSegment(sketch, "E234", {"start": v(12860.87, 8621.71) * mm, "end": v(15123.58, 8621.71) * mm, "construction": true});
            skLineSegment(sketch, "E235", {"start": v(15123.58, 8621.71) * mm, "end": v(17386.3, 8621.71) * mm, "construction": true});
            skPoint(sketch, "E236", {"position": v(16254.94, 10071.1) * mm});
            skSolve(sketch);
        }
    });
